# Revit family: HVAC_HeatPumpAW_Enertech_CTC-EcoAir-700M
name_source: partatom
category: Specialty Equipment
units: mm (PartAtom-declared; Revit-internal decimal feet)

## family parameters
Always vertical = No
Cut with Voids When Loaded = No
OmniClass Number = 23.75.00.00
OmniClass Title = Climate Control (HVAC)
Part Type = Normal
Room Calculation Point = No
Round Connector Dimension = Use Diameter
Shared = No
Work Plane-Based = No

## types (4) — shared parameters
AirFlow nominal (m3/h) = 2787
AssetType = Fixed
BIMObjectName = HVAC_HeatPumpAW_Enertech_CTC-EcoAir-700M
Brand = CTC
BrineSystem_Min_MaxPressure = 0-31
CO2Equivalent = 0.000016
COP min: W35 & A +12 = 6.26
COP min: W35 & A +2 = 4.34
COP min: W35 & A +7 = 5.01
COP min: W35 & A -15 = -
COP min: W35 & A -7 = -
Capacity = Variable
Category = Heat Pumps, Air-to-water
Color = grey/black
CoolingCapacity max: A35 & W18 = 7530 W
CoolingCapacity max: A35 & W7 = 5650 W
CoolingCapacity min: A35 & W18 = 1560 W
CoolingCapacity min: A35 & W7 = 940 W
CoolingCapacity nominal: A35 & W18 = 5240 W
CoolingCapacity nominal: A35 & W7 = 3790 W
Description = CTC EcoAir 700M, a series of speed controlled air-to-water heat pumps with the natural refrigerant R290, which can produce both cooling and heating.
DurationUnit = Year
EER max: A35 & W18 = 2.93
EER max: A35 & W7 = 2.42
EER min: A35 & W18 = 4.42
EER min: A35 & W7 = 2.59
EER nominal: A35 & W18 = 4.02
EER nominal: A35 & W7 = 3.04
ElectricalDeviceNominalPower = 0 W
EnergyClassHeatingWithControl W35 = A+++
EnergyClassHeatingWithControl W55 = A+++
EnergyClassHeatingWithoutControl W35 = A+++
EnergyClassHeatingWithoutControl W55 = A+++
GroupFuse = 16
HasProtectiveEarth = Yes
IP_Code = IP X4
IfcExportAs = IfcElectricalDeviceCommon
IfcExportType = HEATER
InPutPower min: W35 & A +12 = 370 W
InPutPower min: W35 & A +2 = 480 W
InPutPower min: W35 & A +7 = 400 W
InPutPower min: W35 & A -15 = 0 W
InPutPower min: W35 & A -7 = 0 W
KvsValueProduct = 5.34
Manufacturer = CTC AB
ManufacturerCountry = Sweden
ManufacturerName = CTC AB
ManufacturerURL = https://ctc.se
Material = Steel/copper
MaxOperatingPressureThermalStore = 3
NBSDescription = Air to water heat pumps
NBSReference = 90-40-40/320
Name = CTC-EcoAir-700M
NominalCurrent = 0 A
NominalDepth = 513 mm
NominalFrequencyRange = 50 Hz
NominalHeight = 1060 mm  [stored 3.47769 ft]
NominalWidth = 1248 mm  [stored 4.09449 ft]
PhaseAngle = 0.00°
PowerFactor = 0 W
ProductInformation = CTC EcoAir 700M, a series of speed controlled air-to-water heat pumps with the natural refrigerant R290, which can produce both cooling and heating.
PumpMainMaterial = Steel - Grey
RefrigerantQuantity = 0.8
RefrigerantType = R290
Shape = Rectangular
Size = 510x1248x1068
SpecifiedOutput min: W35 & A +12 = 2320 W
SpecifiedOutput min: W35 & A +2 = 2070 W
SpecifiedOutput min: W35 & A +7 = 1990 W
SpecifiedOutput min: W35 & A -15 = 0 W
SpecifiedOutput min: W35 & A -7 = 0 W
Touchscreen = no
UNSPSCCode = 40101806
URL = https://ctc-heating.com
Uniclass2 = Pr_40_70_65
Uniclass2015Description = Preparation catering equipment
Uniclass2015Reference = Pr_40_70_65
UsageCurrent = 0 A
Version = 1
VersionDate = 15/03/2024
WarrantyDurationUnit = Year
WaterVolumeHeathingSystem = 2.9
zero-valued in all types: Cost, Default Elevation

## per-type parameters (varying)
- CTC EcoAir 708M 400V3N: AirFlow max (m3/h)=3041; COP max: W35 & A +12=4.78; COP max: W35 & A +2=3.49; COP max: W35 & A +7=4.05; COP max: W35 & A -15=2.55; COP max: W35 & A -7=3.15; EANNumber=7333077103705; InPutPower max: W35 & A +12=1820 W; InPutPower max: W35 & A +2=1620 W; InPutPower max: W35 & A +7=1720 W; InPutPower max: W35 & A -15=1620 W; InPutPower max: W35 & A -7=1750 W; MaxStartingCurrent=1.1; ModelNumber=590500001; NominalVoltage=400 V; NumberOfPoles=3; RatedCurrent=5 A; RatedHeatOutputCold Pdesigh W35=6000 W; RatedHeatOutputCold Pdesigh W55=6000 W; RatedHeatOutputModerate Pdesigh W35=5000 W; RatedHeatOutputModerate Pdesigh W55=5000 W; RatedHeatOutputWarm Pdesigh W35=6000 W; RatedHeatOutputWarm Pdesigh W55=6000 W; RatedVoltage=1200 V; SCOPCold W35=4.25; SCOPCold W55=3.43; SCOPModerate W35=5.04; SCOPModerate W55=3.85; SCOPWarm W35=6.16; SCOPWarm W55=4.67; Sound pressureLPA 10m=21; Sound pressureLPA 5m=27; SoundPowerLWA=46; SpecifiedOutput max: W35 & A +12=8710 W; SpecifiedOutput max: W35 & A +2=5660 W; SpecifiedOutput max: W35 & A +7=6960 W; SpecifiedOutput max: W35 & A -15=4130 W; SpecifiedOutput max: W35 & A -7=5510 W; Weight=164
- CTC EcoAir 712M 400V3N: AirFlow max (m3/h)=3340; COP max: W35 & A +12=4.33; COP max: W35 & A +2=2.90; COP max: W35 & A +7=3.44; COP max: W35 & A -15=2.27; COP max: W35 & A -7=2.54; EANNumber=7333077103712; InPutPower max: W35 & A +12=2600 W; InPutPower max: W35 & A +2=2540 W; InPutPower max: W35 & A +7=2630 W; InPutPower max: W35 & A -15=2740 W; InPutPower max: W35 & A -7=2080 W; MaxStartingCurrent=1.1; ModelNumber=590510001; NominalVoltage=400 V; NumberOfPoles=3; RatedCurrent=8 A; RatedHeatOutputCold Pdesigh W35=8000 W; RatedHeatOutputCold Pdesigh W55=8000 W; RatedHeatOutputModerate Pdesigh W35=7000 W; RatedHeatOutputModerate Pdesigh W55=7000 W; RatedHeatOutputWarm Pdesigh W35=8000 W; RatedHeatOutputWarm Pdesigh W55=8000 W; RatedVoltage=1200 V; SCOPCold W35=4.24; SCOPCold W55=3.38; SCOPModerate W35=5.00; SCOPModerate W55=3.86; SCOPWarm W35=6.07; SCOPWarm W55=4.48; Sound pressureLPA 10m=22; Sound pressureLPA 5m=28; SoundPowerLWA=47; SpecifiedOutput max: W35 & A +12=11230 W; SpecifiedOutput max: W35 & A +2=7360 W; SpecifiedOutput max: W35 & A +7=9040 W; SpecifiedOutput max: W35 & A -15=6240 W; SpecifiedOutput max: W35 & A -7=7110 W; Weight=164
- CTC EcoAir 708M 230V1N: AirFlow max (m3/h)=3041; COP max: W35 & A +12=4.78; COP max: W35 & A +2=3.49; COP max: W35 & A +7=4.05; COP max: W35 & A -15=2.55; COP max: W35 & A -7=3.15; EANNumber=7333077103743; InPutPower max: W35 & A +12=1820 W; InPutPower max: W35 & A +2=1620 W; InPutPower max: W35 & A +7=1720 W; InPutPower max: W35 & A -15=1620 W; InPutPower max: W35 & A -7=1750 W; MaxStartingCurrent=1.8; ModelNumber=590501001; NominalVoltage=230 V; NumberOfPoles=1; RatedCurrent=16 A; RatedHeatOutputCold Pdesigh W35=6000 W; RatedHeatOutputCold Pdesigh W55=6000 W; RatedHeatOutputModerate Pdesigh W35=5000 W; RatedHeatOutputModerate Pdesigh W55=5000 W; RatedHeatOutputWarm Pdesigh W35=6000 W; RatedHeatOutputWarm Pdesigh W55=6000 W; RatedVoltage=230 V; SCOPCold W35=4.25; SCOPCold W55=3.43; SCOPModerate W35=5.04; SCOPModerate W55=3.85; SCOPWarm W35=6.16; SCOPWarm W55=4.67; Sound pressureLPA 10m=21; Sound pressureLPA 5m=27; SoundPowerLWA=46; SpecifiedOutput max: W35 & A +12=8710 W; SpecifiedOutput max: W35 & A +2=5660 W; SpecifiedOutput max: W35 & A +7=6960 W; SpecifiedOutput max: W35 & A -15=4130 W; SpecifiedOutput max: W35 & A -7=5510 W; Weight=160
- CTC EcoAir 712M 230V1N: AirFlow max (m3/h)=3340; COP max: W35 & A +12=4.33; COP max: W35 & A +2=2.90; COP max: W35 & A +7=3.44; COP max: W35 & A -15=2.27; COP max: W35 & A -7=2.54; EANNumber=7333077103750; InPutPower max: W35 & A +12=2600 W; InPutPower max: W35 & A +2=2540 W; InPutPower max: W35 & A +7=2630 W; InPutPower max: W35 & A -15=2740 W; InPutPower max: W35 & A -7=2080 W; MaxStartingCurrent=1.8; ModelNumber=590511001; NominalVoltage=230 V; NumberOfPoles=1; RatedCurrent=16 A; RatedHeatOutputCold Pdesigh W35=8000 W; RatedHeatOutputCold Pdesigh W55=8000 W; RatedHeatOutputModerate Pdesigh W35=7000 W; RatedHeatOutputModerate Pdesigh W55=7000 W; RatedHeatOutputWarm Pdesigh W35=8000 W; RatedHeatOutputWarm Pdesigh W55=8000 W; RatedVoltage=230 V; SCOPCold W35=4.24; SCOPCold W55=3.38; SCOPModerate W35=5.00; SCOPModerate W55=3.86; SCOPWarm W35=6.07; SCOPWarm W55=4.48; Sound pressureLPA 10m=22; Sound pressureLPA 5m=28; SoundPowerLWA=47; SpecifiedOutput max: W35 & A +12=11230 W; SpecifiedOutput max: W35 & A +2=7360 W; SpecifiedOutput max: W35 & A +7=9040 W; SpecifiedOutput max: W35 & A -15=6240 W; SpecifiedOutput max: W35 & A -7=7110 W; Weight=160

note: column(s) folded — value = type name in every type: Model

note: [stored X ft] marks values corroborated as IEEE doubles in the binary element streams (Revit-internal decimal feet)

## geometry (parser evidence)
native form markers: Sweep x5
no freeform markers — native parametric forms only
